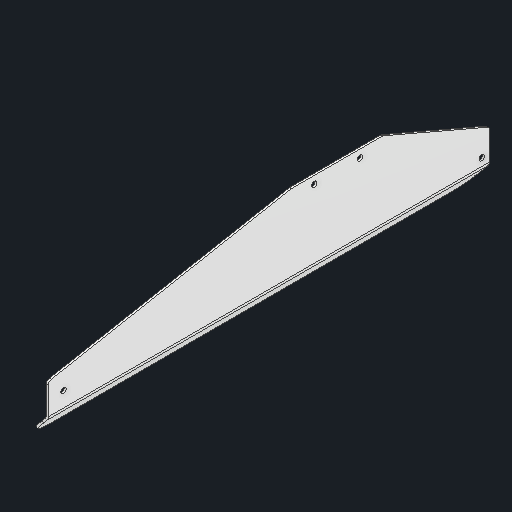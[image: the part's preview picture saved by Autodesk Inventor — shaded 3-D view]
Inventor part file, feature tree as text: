
AUTODESK INVENTOR PART (.ipt)
format: ipt  version: 2025 (Build 290162000, 162)  size: 136,704 bytes
history: native  units: in
note: dims shown in document units (in); Inventor stores cm internally (conversion verified against a paired STEP export)
features: other x4, sketch x1, extrude x1
ambient origin geometry x8: Origin, YZ Plane, XZ Plane, XY Plane, X Axis, Y Axis, Z Axis, Center Point
bodies: Solid1 (feature_tree)
feature tree (6):
  other  "Blocks"
  sketch  "Sketch1"  dims[d0=1.0in d1=0.125in d2=0.125in d3=0.125in d4=1.25in d5=90.0deg d6=1.0in d7=0.5in d8=0.0625in d9=0.0in d10=0.125in d11=0.2749in]
  extrude  "Extrusion1"  Depth=0.0625in TaperAngle=0.0deg
  other  "Bend Part1"
  other  "main"
  other  "main:1"
